# Revit family: HVAC-Chilled_Beam-Dadanco-ACB10
name_source: partatom
category: Mechanical Equipment
revit_build: Autodesk Revit 2015 (Build: 20140903_1530(x64)
units: mm (PartAtom-declared; Revit-internal decimal feet)

## types (4) — shared parameters
0.5 inch Female NPT Stub coil Connection = No
0.5 inch Male NPT Stub Coil Connection = No
0.5 inch SWT Stub Coil Connection = Yes
2 Pipe Coil Configuration = Yes
2 or 4 pipe = 2
4 Pipe Coil Configuration = No
Architectural Design Manual = http://www.activechilledbeam.com
Assembly Code = D3040100
CWF = 0.0 GPM
CWPD = 0.00 ftH2O
Cooling Primary Air Dry Bulb = 0 °F
Cooling Primary Air Wet Bulb = 0 °F
Cooling Room Dry Bulb = 0 °F
Cooling Supply Air Temperature = 0 °F
Damper = Yes
Description = Active Chilled Beam
Documentation Link = http://www.dadanco.com
Drain Pan Material = Metal-Dadanco-Steel-Galvanized Black Powder Coat Finish
Drain Pan Width = 14"
HWF = 0.0 GPM
HWPD = 0.00 ftH2O
Heating Primary Air Dry Bulb = 0 °F
Heating Primary Air Wet Bulb = 0 °F
Heating Room Dry Bulb = 0 °F
Heating Supply Air Temperature = 0 °F
Housing Material = Metal-Dadanco-Steel-Galvanized
Keynote = 23 37 00.A1
Latent Cooling = 0.0 Btu/h
Lint Screen = Yes
Manufacturer = Dadanco
Model = ACB10
Net Unit Cooling Sensible = 0.0 Btu/h
Net Unit Heating Sensible = 0.0 Btu/h
Oval Air Inlet Half Length = 2 1/2"
Oval Air Inlet Height = 2"
Oval Air Inlet Length = 5"
Oval Air Inlet Radius = 1"
PA = 0 CFM
PASP = 0.00 in-wg
Pipe Coil Inlet = 2 Pipe Coi, 0.5 inch SWT Stub Coil Connection
Pipe Coil Outlet = 2 Pipe Coi, 0.5 inch SWT Stub Coil Connection
Primary Air Inlet Size = 4"
Product Page URL = http://www.activechilledbeam.com
Revision Date = 12/28/2010
SCHW Temp Out = 0 °F
SCHW Temperature = 0 °F
SHHW Temp Out = 0 °F
SHHW Temperature = 0 °F
Screen Material = Metal-Dadanco-Aluminum-Screen
Secondary Air Sensible Cooling = 0.0 Btu/h
Secondary Air Sensible Heating = 0.0 Btu/h
Side Air Inlet Round Radius = 2"
Supply Air = 0 CFM
Total Cooling Capacity = 0.0 Btu/h
Type Comments = Horizonatally Mounted Induction Unit
URL = http://www.dadanco.com
Unit Height = 7"
Unit Width = 17"
zero-valued in all types: Cooling Room Relative Humidity

## per-type parameters (varying)
| type | Coil Length | Drain Pan Length | Nominal Unit Length | Overall Unit Length | Unit Length | Unit Weight |
| 4' Nominal Length | 40" | 44" | 48" | 42" | 40" | 42 lb |
| 3' Nominal Length | 32" | 36" | 36" | 34" | 32" | 35 lb |
| 5' Nominal Length | 52" | 56" | 60" | 54" | 52" | 49 lb |
| 6' Nominal Length | 64" | 68" | 72" | 66" | 64" | 56 lb |

## geometry (parser evidence)
native form markers: Sweep x5
no freeform markers — native parametric forms only
